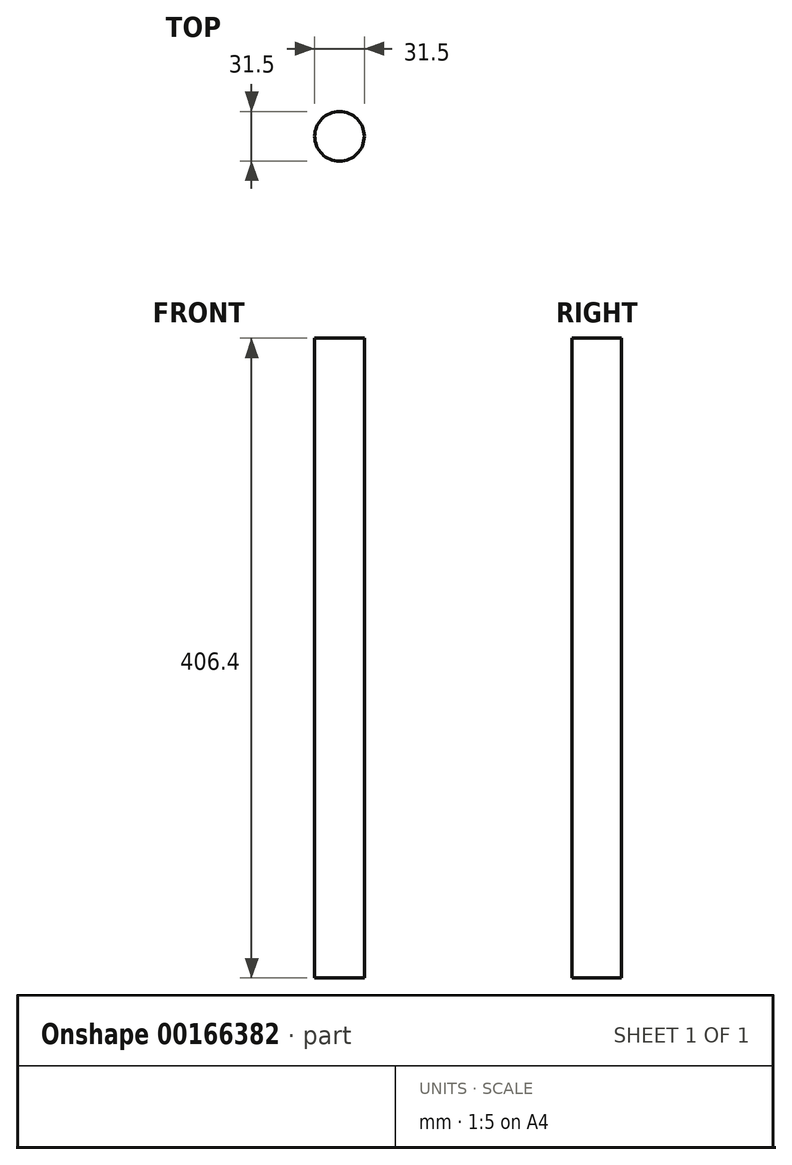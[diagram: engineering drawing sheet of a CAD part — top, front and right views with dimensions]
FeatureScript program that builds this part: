
annotation { "Feature Type Name" : "Feature", "Feature Type Description" : "" }
export const myFeature = defineFeature(function(context is Context, id is Id, definition is map)
    precondition{}
    {
        {
            var Q0;
            Q0=qCreatedBy(makeId("Top.planeOp"),FACE);
            var sketch = newSketch(context, id + "F0", { "sketchPlane" : qUnion([Q0])});
            skCircle(sketch, "E0", {"center": v(0, 0) * mm, "radius": 15.75 * mm});
            skSolve(sketch);
        }
        {
            var Q0;
            Q0=makeQuery(id+"F0.imprint","IMPRINT",FACE,{"disambiguationData":[TD([[makeQuery(id+"F0.imprint","IMPRINT",EDGE,{"derivedFrom":sQuery(id+"F0.wireOp",EDGE,"E0")}),1.0]])]});
            extrude(context, id + "F1", {"entities" : qUnion([Q0]), "depth" : 406.4 * mm});
        }
    });
